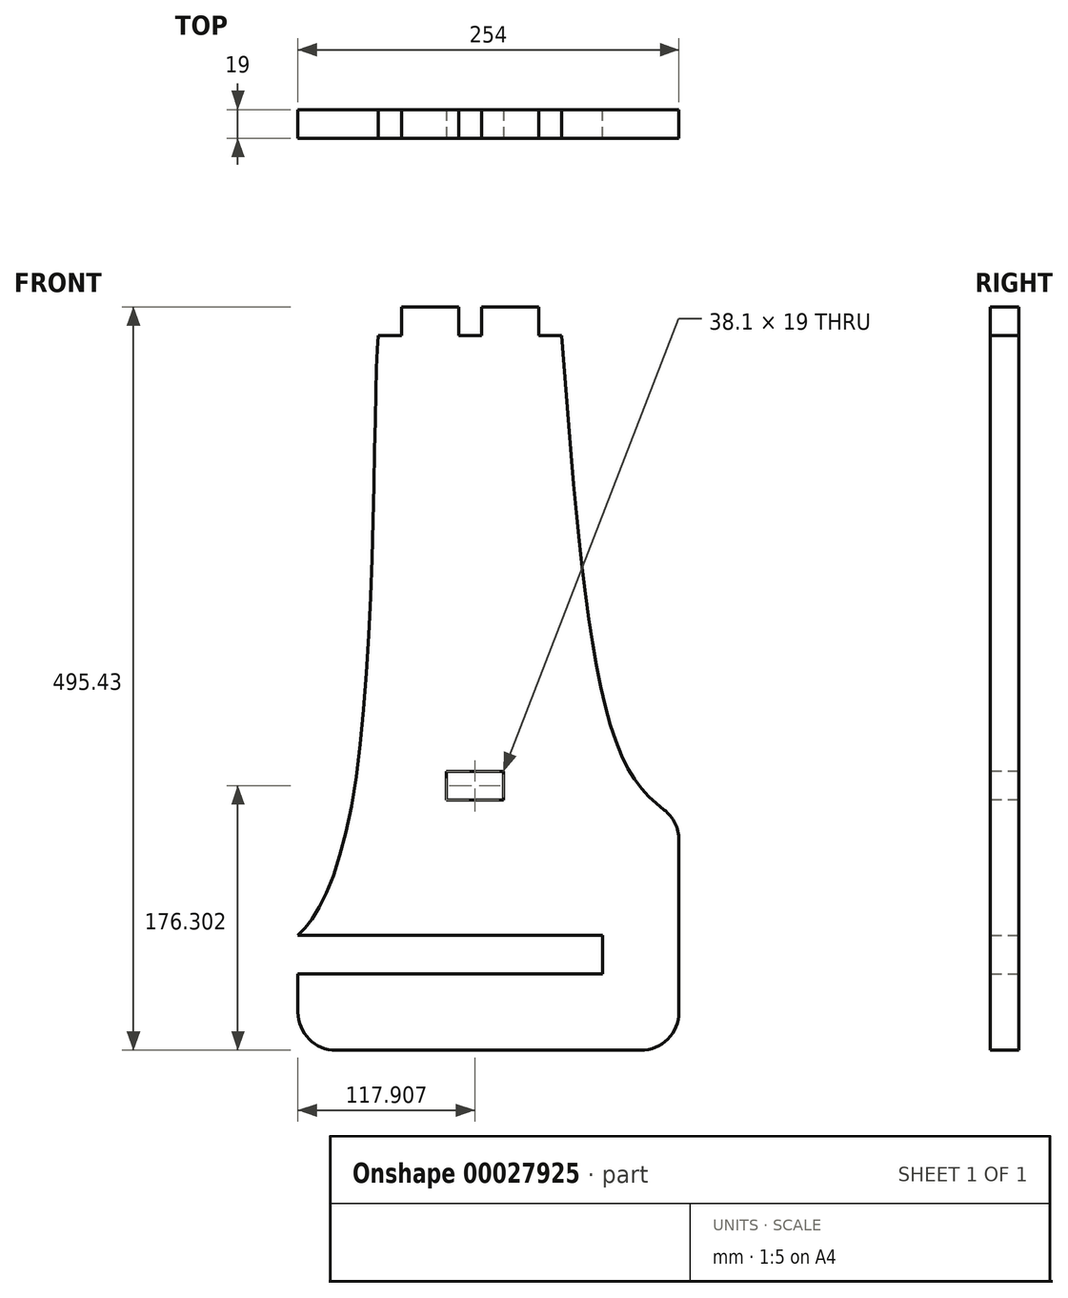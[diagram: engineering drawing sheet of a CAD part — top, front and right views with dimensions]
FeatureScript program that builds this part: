
annotation { "Feature Type Name" : "Feature", "Feature Type Description" : "" }
export const myFeature = defineFeature(function(context is Context, id is Id, definition is map)
    precondition{}
    {
        {
            var Q0;
            Q0=qCreatedBy(makeId("Front.planeOp"),FACE);
            var sketch = newSketch(context, id + "F0", { "sketchPlane" : qUnion([Q0])});
            skLineSegment(sketch, "E0", {"start": v(17.72, 0) * mm, "end": v(67.54, 0) * mm});
            skLineSegment(sketch, "E1", {"start": v(67.54, 0) * mm, "end": v(67.54, -25.8) * mm});
            skLineSegment(sketch, "E2", {"start": v(67.54, -25.8) * mm, "end": v(-135.66, -25.8) * mm});
            skLineSegment(sketch, "E3", {"start": v(-135.66, -76.6) * mm, "end": v(118.34, -76.6) * mm});
            skPoint(sketch, "E4.start.orphan", {"position": v(-135.66, 0) * mm});
            skPoint(sketch, "E5.orphan", {"position": v(0, 0) * mm});
            skLineSegment(sketch, "E6", {"start": v(17.72, 0) * mm, "end": v(-135.66, 0) * mm});
            skLineSegment(sketch, "E7", {"start": v(-135.66, -25.8) * mm, "end": v(-135.66, -76.6) * mm});
            skPoint(sketch, "E8.end.orphan", {"position": v(-179.83, -25.8) * mm});
            skFitSpline(sketch, "E9", {"points": [v(-135.66, 0) * mm, v(-97.83, 98.73) * mm, v(-81.75, 402.07) * mm], "startDerivative": vector(108.8, 91.31) * mm, "endDerivative": vector(19.37, 136.4) * mm});
            skLineSegment(sketch, "E10", {"start": v(40.17, 399.83) * mm, "end": v(-82.03, 399.83) * mm});
            skLineSegment(sketch, "E11", {"start": v(-66.51, 399.83) * mm, "end": v(-66.51, 418.83) * mm});
            skLineSegment(sketch, "E12", {"start": v(-66.51, 418.83) * mm, "end": v(-28.41, 418.83) * mm});
            skLineSegment(sketch, "E13", {"start": v(-28.41, 418.83) * mm, "end": v(-28.41, 399.83) * mm});
            skLineSegment(sketch, "E14", {"start": v(-28.41, 399.83) * mm, "end": v(-13.17, 399.83) * mm});
            skLineSegment(sketch, "E15", {"start": v(-13.17, 399.83) * mm, "end": v(-13.17, 418.83) * mm});
            skLineSegment(sketch, "E16", {"start": v(-13.17, 418.83) * mm, "end": v(24.93, 418.83) * mm});
            skLineSegment(sketch, "E17", {"start": v(24.93, 418.83) * mm, "end": v(24.93, 399.83) * mm});
            skFitSpline(sketch, "E18", {"points": [v(40.17, 399.83) * mm, v(81.39, 116.86) * mm, v(118.34, 76.53) * mm], "startDerivative": vector(37.6, -502.13) * mm, "endDerivative": vector(130.92, -90.82) * mm});
            skLineSegment(sketch, "E19", {"start": v(118.34, 76.53) * mm, "end": v(118.34, -76.6) * mm});
            skSolve(sketch);
        }
        {
            var Q0;
            Q0=qSketchRegion(id+"F0",true);
            extrude(context, id + "F1", {"entities" : qUnion([Q0]), "depth" : 19 * mm});
        }
        {
            var Q0;
            Q0=makeQuery(id+"F1.opExtrude","CAP_FACE",FACE,{"disambiguationData":[OSD([sQuery(id+"F0.wireOp",EDGE,"E0"),sQuery(id+"F0.wireOp",EDGE,"E1"),sQuery(id+"F0.wireOp",EDGE,"E2"),sQuery(id+"F0.wireOp",EDGE,"E3"),sQuery(id+"F0.wireOp",EDGE,"E6"),sQuery(id+"F0.wireOp",EDGE,"d77e7821-c080-4193-9de1-063b469677b2"),sQuery(id+"F0.wireOp",EDGE,"E7"),sQuery(id+"F0.wireOp",EDGE,"E9"),sQuery(id+"F0.wireOp",EDGE,"E10"),sQuery(id+"F0.wireOp",EDGE,"E11"),sQuery(id+"F0.wireOp",EDGE,"E12"),sQuery(id+"F0.wireOp",EDGE,"E13"),sQuery(id+"F0.wireOp",EDGE,"E14"),sQuery(id+"F0.wireOp",EDGE,"E15"),sQuery(id+"F0.wireOp",EDGE,"E16"),sQuery(id+"F0.wireOp",EDGE,"E17"),sQuery(id+"F0.wireOp",EDGE,"7822a1e9-162b-4067-a8fa-4ee3e35ef97c")])],"isStart":false});
            var sketch = newSketch(context, id + "F2", { "sketchPlane" : qUnion([Q0])});
            skLineSegment(sketch, "E20.rect.bottom", {"start": v(1.3, 90.2) * mm, "end": v(-36.8, 90.2) * mm});
            skLineSegment(sketch, "E20.rect.top", {"start": v(1.3, 109.2) * mm, "end": v(-36.8, 109.2) * mm});
            skLineSegment(sketch, "E20.rect.left", {"start": v(1.3, 90.2) * mm, "end": v(1.3, 109.2) * mm});
            skLineSegment(sketch, "E20.rect.right", {"start": v(-36.8, 90.2) * mm, "end": v(-36.8, 109.2) * mm});
            skPoint(sketch, "E20.rect.middle", {"position": v(-17.75, 99.7) * mm});
            skSolve(sketch);
        }
        {
            var Q0;
            Q0=makeQuery(id+"F2.imprint","IMPRINT",FACE,{"disambiguationData":[TD([[makeQuery(id+"F2.imprint","IMPRINT",EDGE,{"derivedFrom":sQuery(id+"F2.wireOp",EDGE,"E20.rect.bottom")}),-1.0]])]});
            extrude(context, id + "F3", {"entities" : qUnion([Q0]), "operationType" : NewBodyOperationType.REMOVE, "oppositeDirection" : true, "depth" : 19 * mm});
        }
        {
            var Q0;
            Q0=makeQuery(id+"F1.opExtrude","SWEPT_EDGE",EDGE,{"disambiguationData":[OSD([sQuery(id+"F0.wireOp",EDGE,"E3"),sQuery(id+"F0.wireOp",EDGE,"E7")])]});
            var Q1;
            Q1=makeQuery(id+"F1.opExtrude","SWEPT_EDGE",EDGE,{"disambiguationData":[OSD([sQuery(id+"F0.wireOp",EDGE,"d77e7821-c080-4193-9de1-063b469677b2"),sQuery(id+"F0.wireOp",EDGE,"7822a1e9-162b-4067-a8fa-4ee3e35ef97c")])]});
            var Q2;
            Q2=makeQuery(id+"F1.opExtrude","SWEPT_EDGE",EDGE,{"disambiguationData":[OSD([sQuery(id+"F0.wireOp",EDGE,"E3"),sQuery(id+"F0.wireOp",EDGE,"7822a1e9-162b-4067-a8fa-4ee3e35ef97c")])]});
            var Q3;
            Q3=makeQuery(id+"F1.opExtrude","SWEPT_EDGE",EDGE,{"disambiguationData":[OSD([sQuery(id+"F0.wireOp",EDGE,"E18"),sQuery(id+"F0.wireOp",EDGE,"E19")])]});
            fillet(context, id + "F4", {"entities" : qUnion([Q0, Q1, Q2, Q3]), "radius" : 25.4 * mm, "tangentPropagation" : true, "allowEdgeOverflow" : false});
        }
    });
